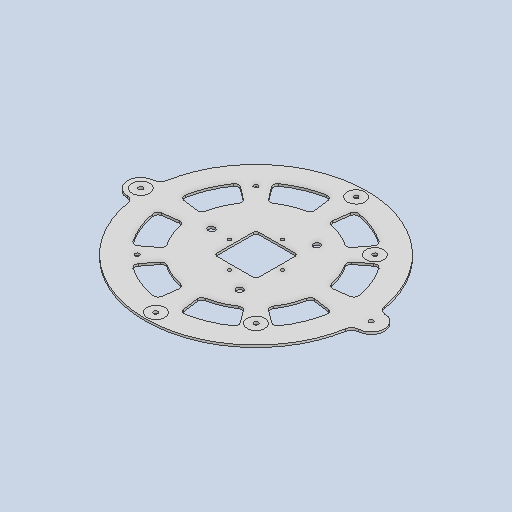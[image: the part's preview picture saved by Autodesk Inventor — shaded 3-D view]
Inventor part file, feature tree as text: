
AUTODESK INVENTOR PART (.ipt)
format: ipt  version: 2025.1 (Build 291241020, 241B)  size: 944,128 bytes
history: native  units: in
note: dims shown in document units (in); Inventor stores cm internally (conversion verified against a paired STEP export)
features: sketch x8, extrude x5, split x3, fillet x2
ambient origin geometry x8: Origin, YZ Plane, XZ Plane, XY Plane, X Axis, Y Axis, Z Axis, Center Point
bodies: Solid35 (feature_tree), Solid40 (feature_tree), Solid41 (feature_tree)
feature tree (18):
  extrude  "Extrusion1"  Depth=2.3661in
  fillet  "Fillet1"  Radius=2.3661in
  extrude  "Extrusion3"  Depth=2.3661in
  extrude  "Extrusion2"  Depth=0.1575in
  fillet  "Fillet5"  Radius=0.201in
  sketch  "Sketch5"  dims[d10=0.201in d11=2.9921in]
  split  "Split17"
  split  "Split18"
  split  "Split19"
  sketch  "Sketch8"  dims[d13=2.9921in]
  sketch  "Sketch9"  dims[d14=1.4961in d15=0.375in d17=4.358in d20=0.375in d24=0.2525in d25=0.2525in d26=11.311in d27=5.6555in d30=1.5in d31=0.2525in d33=13.01in d34=0.125in d35=0.0in d36=0.4in d38=4.358in d39=4.358in d41=5.0322in d54=0.25in d55=0.0in d79=0.25in d80=0.25in d81=0.25in d82=0.25in d83=9.5in d84=6.7175in d85=6.7175in d86=9.5in d87=0.25in d88=0.0in d94=3.3588in d95=3.3588in d96=10.0in d97=7.25in d98=15.0deg d99=0.2577in d100=3.1496in d102=360.0deg d104=0.25in d107=0.125in d108=0.125in d109=0.125in d119=0.4573in d120=0.4162in d121=0.3519in d122=0.6651in d123=0.379in d124=0.2188in d125=0.383in d126=0.735in d127=0.5332in d128=0.2522in d129=0.3287in d130=0.0218in d131=0.125in d132=0.3485in d133=0.0777in d135=1.0in d136=1.0in d137=1.0in d138=1.0in d139=1.0in d140=1.0in d141=1.0in d142=1.0in d143=0.0in d144=0.0in d145=0.0in d146=0.0in d147=1.0in d148=1.0in d149=1.0in d150=1.0in]
  extrude  "Extrusion4"  Depth=0.201in
  extrude  "Extrusion5"  Depth=2.9921in
  sketch  "Sketch1"  dims[d0=12.5in d1=1.1831in d2=2.3661in]
  sketch  "Sketch2"  dims[d3=2.3661in d4=1.1831in]
  sketch  "Sketch4"  dims[d5=0.1575in d6=0.1575in d7=0.201in]
  sketch  "Sketch Circular Pattern4"  dims[d8=0.201in d9=0.201in]
  sketch  "Sketch6"  dims[d12=1.4961in]
